# Revit family: DCST_Счетчик тепла бытовой_СТК МАРС NEO RF
name_source: partatom
category: Арматура трубопроводов
units: mm (PartAtom-declared; Revit-internal decimal feet)

## family parameters
Всегда вертикально = Да
На основе рабочей плоскости = Нет
Общий = Нет
При загрузке вырезать с полостями = Нет
Размер круглого соединителя = Использовать диаметр
Тип детали = Вставляется

## types (4) — shared parameters
ADSK_Единица измерения = шт.
ADSK_Завод-изготовитель = Декаст
ADSK_Количество = 1
D1 = 15 мм
LT = СТК МАРС NEO RF
Q1 = ♠ : Qn = 0.6 м³/ч
Q2 = ♠ : Qn = 1.0 м³/ч
Q3 = ♠ : Qn = 1.5 м³/ч
Q4 = ♠ : Qn = 2.5 м³/ч
URL = https://www.decast.com
Изготовитель = Декаст

## per-type parameters (varying)
| type | ADSK_Диаметр условный | D | D2 | Диаметр условного прохода | Диаметр штуцера | Длина гаек | Длина штуцера | Монтажная длина | Обратная магистраль | Размер под ключ | УГО_Высота | УГО_Длина | УГО_Длина линии |
| СТК МАРС NEO-15 RF Подача | 15 мм | 18 мм | 10 мм | 15 мм | 18 мм | 14 мм | 35 мм | 110 мм | Нет | 30 мм | 55 мм | 110 мм | 35 мм |
| СТК МАРС NEO-15 RF Обратка | 15 мм | 18 мм | 10 мм | 15 мм | 18 мм | 14 мм | 35 мм | 110 мм | Да | 30 мм | 55 мм | 110 мм | 35 мм |
| СТК МАРС NEO-20 RF Подача | 20 мм | 25 мм | 18 мм | 20 мм | 25 мм | 17 мм | 50 мм | 130 мм | Нет | 35 мм | 65 мм | 130 мм | 50 мм |
| СТК МАРС NEO-20 RF Обратка | 20 мм | 25 мм | 18 мм | 20 мм | 25 мм | 17 мм | 50 мм | 130 мм | Да | 35 мм | 65 мм | 130 мм | 50 мм |
